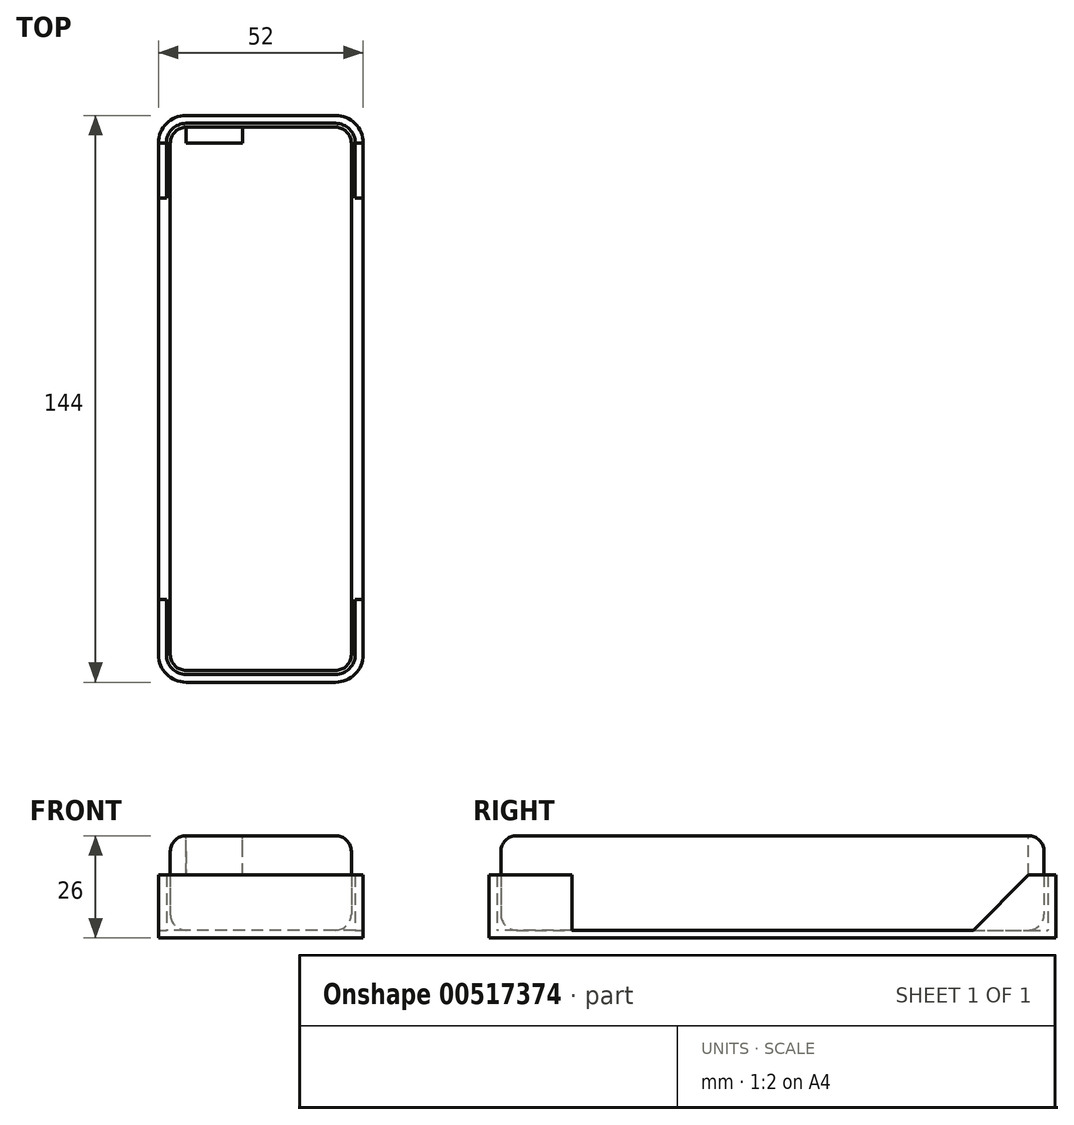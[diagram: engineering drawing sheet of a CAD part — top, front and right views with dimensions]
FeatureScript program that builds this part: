
annotation { "Feature Type Name" : "Feature", "Feature Type Description" : "" }
export const myFeature = defineFeature(function(context is Context, id is Id, definition is map)
    precondition{}
    {
        {
            var Q0;
            Q0=qCreatedBy(makeId("Top.planeOp"),FACE);
            var sketch = newSketch(context, id + "F0", { "sketchPlane" : qUnion([Q0])});
            skLineSegment(sketch, "E0.bottom", {"start": v(-4, 0) * mm, "end": v(-42, 0) * mm});
            skLineSegment(sketch, "E0.top", {"start": v(-4, 138) * mm, "end": v(-42, 138) * mm});
            skLineSegment(sketch, "E0.left", {"start": v(0, 4) * mm, "end": v(0, 134) * mm});
            skLineSegment(sketch, "E0.right", {"start": v(-46, 4) * mm, "end": v(-46, 134) * mm});
            skPoint(sketch, "E1.visualSharp", {"position": v(-46, 0) * mm});
            skArc(sketch, "E1.filletArc", {"start": v(-46, 4) * mm, "mid": v(-44.83, 1.17) * mm, "end": v(-42, 0) * mm});
            skPoint(sketch, "E2.visualSharp", {"position": v(0, 0) * mm});
            skArc(sketch, "E2.filletArc", {"start": v(-4, 0) * mm, "mid": v(-1.17, 1.17) * mm, "end": v(0, 4) * mm});
            skPoint(sketch, "E3.visualSharp", {"position": v(-46, 138) * mm});
            skArc(sketch, "E3.filletArc", {"start": v(-42, 138) * mm, "mid": v(-44.83, 136.83) * mm, "end": v(-46, 134) * mm});
            skPoint(sketch, "E4.visualSharp", {"position": v(0, 138) * mm});
            skArc(sketch, "E4.filletArc", {"start": v(0, 134) * mm, "mid": v(-1.17, 136.83) * mm, "end": v(-4, 138) * mm});
            skArc(sketch, "E5.0", {"start": v(-4, -3) * mm, "mid": v(0.95, -0.95) * mm, "end": v(3, 4) * mm});
            skLineSegment(sketch, "E5.1", {"start": v(-4, -3) * mm, "end": v(-42, -3) * mm});
            skLineSegment(sketch, "E5.2", {"start": v(3, 4) * mm, "end": v(3, 134) * mm});
            skArc(sketch, "E5.3", {"start": v(-49, 4) * mm, "mid": v(-46.95, -0.95) * mm, "end": v(-42, -3) * mm});
            skArc(sketch, "E5.4", {"start": v(3, 134) * mm, "mid": v(0.95, 138.95) * mm, "end": v(-4, 141) * mm});
            skLineSegment(sketch, "E5.5", {"start": v(-4, 141) * mm, "end": v(-42, 141) * mm});
            skArc(sketch, "E5.6", {"start": v(-42, 141) * mm, "mid": v(-46.95, 138.95) * mm, "end": v(-49, 134) * mm});
            skLineSegment(sketch, "E5.7", {"start": v(-49, 4) * mm, "end": v(-49, 134) * mm});
            skArc(sketch, "E6.0", {"start": v(-47, 4) * mm, "mid": v(-45.54, 0.46) * mm, "end": v(-42, -1) * mm});
            skLineSegment(sketch, "E6.1", {"start": v(-4, -1) * mm, "end": v(-42, -1) * mm});
            skLineSegment(sketch, "E6.2", {"start": v(-47, 4) * mm, "end": v(-47, 134) * mm});
            skArc(sketch, "E6.3", {"start": v(-4, -1) * mm, "mid": v(-0.46, 0.46) * mm, "end": v(1, 4) * mm});
            skArc(sketch, "E6.4", {"start": v(-42, 139) * mm, "mid": v(-45.54, 137.54) * mm, "end": v(-47, 134) * mm});
            skLineSegment(sketch, "E6.5", {"start": v(-4, 139) * mm, "end": v(-42, 139) * mm});
            skArc(sketch, "E6.6", {"start": v(1, 134) * mm, "mid": v(-0.46, 137.54) * mm, "end": v(-4, 139) * mm});
            skLineSegment(sketch, "E6.7", {"start": v(1, 4) * mm, "end": v(1, 134) * mm});
            skSolve(sketch);
        }
        {
            var Q0;
            Q0=makeQuery(id+"F0.imprint","IMPRINT",FACE,{"disambiguationData":[TD([[makeQuery(id+"F0.imprint","IMPRINT",EDGE,{"derivedFrom":sQuery(id+"F0.wireOp",EDGE,"E0.bottom")}),-1.0]])]});
            extrude(context, id + "F1", {"entities" : qUnion([Q0]), "depth" : 24 * mm, "offsetDistance" : 25 * mm});
        }
        {
            var Q0;
            Q0=makeQuery(id+"F1.opExtrude","CAP_FACE",FACE,{"disambiguationData":[OSD([sQuery(id+"F0.wireOp",EDGE,"E0.bottom"),sQuery(id+"F0.wireOp",EDGE,"E0.top"),sQuery(id+"F0.wireOp",EDGE,"E0.left"),sQuery(id+"F0.wireOp",EDGE,"E0.right"),sQuery(id+"F0.wireOp",EDGE,"E1.filletArc"),sQuery(id+"F0.wireOp",EDGE,"E2.filletArc"),sQuery(id+"F0.wireOp",EDGE,"E3.filletArc"),sQuery(id+"F0.wireOp",EDGE,"E4.filletArc")])],"isStart":false});
            var Q1;
            Q1=makeQuery(id+"F1.opExtrude","CAP_FACE",FACE,{"disambiguationData":[OSD([sQuery(id+"F0.wireOp",EDGE,"E0.bottom"),sQuery(id+"F0.wireOp",EDGE,"E0.top"),sQuery(id+"F0.wireOp",EDGE,"E0.left"),sQuery(id+"F0.wireOp",EDGE,"E0.right"),sQuery(id+"F0.wireOp",EDGE,"E1.filletArc"),sQuery(id+"F0.wireOp",EDGE,"E2.filletArc"),sQuery(id+"F0.wireOp",EDGE,"E3.filletArc"),sQuery(id+"F0.wireOp",EDGE,"E4.filletArc")])],"isStart":true});
            fillet(context, id + "F2", {"entities" : qUnion([Q0, Q1]), "radius" : 4 * mm, "tangentPropagation" : true, "allowEdgeOverflow" : false});
        }
        {
            var Q0;
            Q0=makeQuery(id+"F1.opExtrude","CAP_FACE",FACE,{"disambiguationData":[OSD([sQuery(id+"F0.wireOp",EDGE,"E0.bottom"),sQuery(id+"F0.wireOp",EDGE,"E0.top"),sQuery(id+"F0.wireOp",EDGE,"E0.left"),sQuery(id+"F0.wireOp",EDGE,"E0.right"),sQuery(id+"F0.wireOp",EDGE,"E1.filletArc"),sQuery(id+"F0.wireOp",EDGE,"E2.filletArc"),sQuery(id+"F0.wireOp",EDGE,"E3.filletArc"),sQuery(id+"F0.wireOp",EDGE,"E4.filletArc")])],"isStart":false});
            var sketch = newSketch(context, id + "F3", { "sketchPlane" : qUnion([Q0])});
            skLineSegment(sketch, "E7.bottom", {"start": v(-42, 134) * mm, "end": v(-27.63, 134) * mm});
            skLineSegment(sketch, "E7.top", {"start": v(-42, 138.18) * mm, "end": v(-27.63, 138.18) * mm});
            skLineSegment(sketch, "E7.left", {"start": v(-42, 134) * mm, "end": v(-42, 138.18) * mm});
            skLineSegment(sketch, "E7.right", {"start": v(-27.63, 134) * mm, "end": v(-27.63, 138.18) * mm});
            skSolve(sketch);
        }
        {
            var Q0;
            Q0=makeQuery(id+"F3.imprint","IMPRINT",FACE,{"disambiguationData":[TD([[makeQuery(id+"F3.imprint","IMPRINT",EDGE,{"derivedFrom":sQuery(id+"F3.wireOp",EDGE,"E7.bottom")}),-1.0]])]});
            extrude(context, id + "F4", {"entities" : qUnion([Q0]), "operationType" : NewBodyOperationType.REMOVE, "oppositeDirection" : true, "depth" : 10 * mm, "offsetDistance" : 25 * mm});
        }
        {
            var Q0;
            Q0=makeQuery(id+"F0.imprint","IMPRINT",FACE,{"disambiguationData":[TD([[makeQuery(id+"F0.imprint","IMPRINT",EDGE,{"derivedFrom":sQuery(id+"F0.wireOp",EDGE,"E5.0")}),1.0]])]});
            extrude(context, id + "F5", {"entities" : qUnion([Q0]), "depth" : 14 * mm, "offsetDistance" : 25 * mm});
        }
        {
            var Q0;
            Q0=makeQuery(id+"F0.imprint","IMPRINT",FACE,{"disambiguationData":[TD([[makeQuery(id+"F0.imprint","IMPRINT",EDGE,{"derivedFrom":sQuery(id+"F0.wireOp",EDGE,"E5.0")}),1.0]])]});
            var Q1;
            Q1=makeQuery(id+"F0.imprint","IMPRINT",FACE,{"disambiguationData":[TD([[makeQuery(id+"F0.imprint","IMPRINT",EDGE,{"derivedFrom":sQuery(id+"F0.wireOp",EDGE,"E0.bottom")}),-1.0]])]});
            extrude(context, id + "F6", {"entities" : qUnion([Q0, Q1]), "oppositeDirection" : true, "depth" : 2 * mm, "offsetDistance" : 25 * mm});
        }
        {
            var Q0;
            Q0=makeQuery(id+"F0.imprint","IMPRINT",FACE,{"disambiguationData":[TD([[makeQuery(id+"F0.imprint","IMPRINT",EDGE,{"derivedFrom":sQuery(id+"F0.wireOp",EDGE,"E0.bottom")}),1.0]])]});
            extrude(context, id + "F7", {"entities" : qUnion([Q0]), "operationType" : NewBodyOperationType.ADD, "oppositeDirection" : true, "depth" : 2 * mm, "offsetDistance" : 25 * mm});
        }
        {
            var Q0;
            Q0=makeQuery(id+"F5.opExtrude","CAP_FACE",FACE,{"disambiguationData":[OSD([sQuery(id+"F0.wireOp",EDGE,"E5.0"),sQuery(id+"F0.wireOp",EDGE,"E5.1"),sQuery(id+"F0.wireOp",EDGE,"E5.2"),sQuery(id+"F0.wireOp",EDGE,"E5.3"),sQuery(id+"F0.wireOp",EDGE,"E5.4"),sQuery(id+"F0.wireOp",EDGE,"E5.5"),sQuery(id+"F0.wireOp",EDGE,"E5.6"),sQuery(id+"F0.wireOp",EDGE,"E5.7"),sQuery(id+"F0.wireOp",EDGE,"E6.0"),sQuery(id+"F0.wireOp",EDGE,"E6.1"),sQuery(id+"F0.wireOp",EDGE,"E6.2"),sQuery(id+"F0.wireOp",EDGE,"E6.3"),sQuery(id+"F0.wireOp",EDGE,"E6.4"),sQuery(id+"F0.wireOp",EDGE,"E6.5"),sQuery(id+"F0.wireOp",EDGE,"E6.6"),sQuery(id+"F0.wireOp",EDGE,"E6.7")])],"isStart":false});
            var sketch = newSketch(context, id + "F8", { "sketchPlane" : qUnion([Q0])});
            skLineSegment(sketch, "E8.bottom", {"start": v(-49, 134) * mm, "end": v(3, 134) * mm});
            skLineSegment(sketch, "E8.top", {"start": v(-49, 4) * mm, "end": v(3, 4) * mm});
            skLineSegment(sketch, "E8.left", {"start": v(-49, 134) * mm, "end": v(-49, 4) * mm});
            skLineSegment(sketch, "E8.right", {"start": v(3, 134) * mm, "end": v(3, 4) * mm});
            skSolve(sketch);
        }
        {
            var Q0;
            {var subQ0=sQuery(id+"F8.wireOp",EDGE,"E8.left");Q0=makeQuery(id+"F8.imprint","IMPRINT",FACE,{"disambiguationData":[TD([[makeQuery(id+"F8.imprint","IMPRINT",EDGE,{"derivedFrom":subQ0}),-1.0]])]});}
            var Q1;
            {var subQ0=sQuery(id+"F8.wireOp",EDGE,"E8.right");Q1=makeQuery(id+"F8.imprint","IMPRINT",FACE,{"disambiguationData":[TD([[makeQuery(id+"F8.imprint","IMPRINT",EDGE,{"derivedFrom":subQ0}),1.0]])]});}
            extrude(context, id + "F9", {"entities" : qUnion([Q0, Q1]), "operationType" : NewBodyOperationType.REMOVE, "oppositeDirection" : true, "depth" : 14 * mm, "offsetDistance" : 25 * mm});
        }
        {
            var Q0;
            {var subQ0=sQuery(id+"F8.wireOp",EDGE,"E8.top");Q0=makeQuery(id+"F9.boolean.opBoolean","COPY",FACE,{"derivedFrom":makeQuery(id+"F9.opExtrude","SWEPT_FACE",FACE,{"disambiguationData":[OSD([subQ0]),TDD([makeQuery(id+"F8.imprint","IMPRINT",EDGE,{"disambiguationData":[TD([[makeQuery(id+"F8.imprint","INTERSECT",VERTEX,{"derivedFrom":[makeQuery(id+"F5.opExtrude","CAP_EDGE",EDGE,{"disambiguationData":[OSD([sQuery(id+"F0.wireOp",EDGE,"E5.3")])],"isStart":false}),subQ0,sQuery(id+"F8.wireOp",EDGE,"E8.left")]}),-1.0]])],"derivedFrom":subQ0})])]})});}
            var Q1;
            {var subQ0=sQuery(id+"F8.wireOp",EDGE,"E8.top");Q1=makeQuery(id+"F9.boolean.opBoolean","COPY",FACE,{"derivedFrom":makeQuery(id+"F9.opExtrude","SWEPT_FACE",FACE,{"disambiguationData":[OSD([subQ0]),TDD([makeQuery(id+"F8.imprint","IMPRINT",EDGE,{"disambiguationData":[TD([[makeQuery(id+"F8.imprint","INTERSECT",VERTEX,{"derivedFrom":[makeQuery(id+"F5.opExtrude","CAP_EDGE",EDGE,{"disambiguationData":[OSD([sQuery(id+"F0.wireOp",EDGE,"E5.0")])],"isStart":false}),subQ0,sQuery(id+"F8.wireOp",EDGE,"E8.right")]}),1.0]])],"derivedFrom":subQ0})])]})});}
            extrude(context, id + "F10", {"entities" : qUnion([Q0, Q1]), "operationType" : NewBodyOperationType.ADD, "depth" : 14 * mm, "offsetDistance" : 25 * mm});
        }
        {
            var Q0;
            {var subQ0=sQuery(id+"F8.wireOp",EDGE,"E8.bottom");Q0=makeQuery(id+"F9.boolean.opBoolean","COPY",FACE,{"derivedFrom":makeQuery(id+"F9.opExtrude","SWEPT_FACE",FACE,{"disambiguationData":[OSD([subQ0]),TDD([makeQuery(id+"F8.imprint","IMPRINT",EDGE,{"disambiguationData":[TD([[makeQuery(id+"F8.imprint","INTERSECT",VERTEX,{"derivedFrom":[makeQuery(id+"F5.opExtrude","CAP_EDGE",EDGE,{"disambiguationData":[OSD([sQuery(id+"F0.wireOp",EDGE,"E5.4")])],"isStart":false}),subQ0,sQuery(id+"F8.wireOp",EDGE,"E8.right")]}),1.0]])],"derivedFrom":subQ0})])]})});}
            var Q1;
            {var subQ0=sQuery(id+"F8.wireOp",EDGE,"E8.bottom");Q1=makeQuery(id+"F9.boolean.opBoolean","COPY",FACE,{"derivedFrom":makeQuery(id+"F9.opExtrude","SWEPT_FACE",FACE,{"disambiguationData":[OSD([subQ0]),TDD([makeQuery(id+"F8.imprint","IMPRINT",EDGE,{"disambiguationData":[TD([[makeQuery(id+"F8.imprint","INTERSECT",VERTEX,{"derivedFrom":[makeQuery(id+"F5.opExtrude","CAP_EDGE",EDGE,{"disambiguationData":[OSD([sQuery(id+"F0.wireOp",EDGE,"E5.6")])],"isStart":false}),subQ0,sQuery(id+"F8.wireOp",EDGE,"E8.left")]}),-1.0]])],"derivedFrom":subQ0})])]})});}
            extrude(context, id + "F11", {"entities" : qUnion([Q0, Q1]), "operationType" : NewBodyOperationType.ADD, "depth" : 14 * mm, "offsetDistance" : 25 * mm});
        }
        {
            var Q0;
            {var subQ0=sQuery(id+"F8.wireOp",EDGE,"E8.bottom");Q0=makeQuery(id+"F11.opExtrude","CAP_EDGE",EDGE,{"disambiguationData":[OSD([subQ0]),TDD([makeQuery(id+"F9.boolean.opBoolean","COPY",EDGE,{"derivedFrom":makeQuery(id+"F9.opExtrude","CAP_EDGE",EDGE,{"disambiguationData":[OSD([subQ0]),TDD([makeQuery(id+"F8.imprint","IMPRINT",EDGE,{"disambiguationData":[TD([[makeQuery(id+"F8.imprint","INTERSECT",VERTEX,{"derivedFrom":[makeQuery(id+"F5.opExtrude","CAP_EDGE",EDGE,{"disambiguationData":[OSD([sQuery(id+"F0.wireOp",EDGE,"E5.6")])],"isStart":false}),subQ0,sQuery(id+"F8.wireOp",EDGE,"E8.left")]}),-1.0]])],"derivedFrom":subQ0})])],"isStart":true})})])],"isStart":false});}
            var Q1;
            {var subQ0=sQuery(id+"F8.wireOp",EDGE,"E8.bottom");Q1=makeQuery(id+"F11.opExtrude","CAP_EDGE",EDGE,{"disambiguationData":[OSD([subQ0]),TDD([makeQuery(id+"F9.boolean.opBoolean","COPY",EDGE,{"derivedFrom":makeQuery(id+"F9.opExtrude","CAP_EDGE",EDGE,{"disambiguationData":[OSD([subQ0]),TDD([makeQuery(id+"F8.imprint","IMPRINT",EDGE,{"disambiguationData":[TD([[makeQuery(id+"F8.imprint","INTERSECT",VERTEX,{"derivedFrom":[makeQuery(id+"F5.opExtrude","CAP_EDGE",EDGE,{"disambiguationData":[OSD([sQuery(id+"F0.wireOp",EDGE,"E5.4")])],"isStart":false}),subQ0,sQuery(id+"F8.wireOp",EDGE,"E8.right")]}),1.0]])],"derivedFrom":subQ0})])],"isStart":true})})])],"isStart":false});}
            var Q2;
            {var subQ0=sQuery(id+"F8.wireOp",EDGE,"E8.top");Q2=makeQuery(id+"F10.opExtrude","CAP_EDGE",EDGE,{"disambiguationData":[OSD([subQ0]),TDD([makeQuery(id+"F9.boolean.opBoolean","COPY",EDGE,{"derivedFrom":makeQuery(id+"F9.opExtrude","CAP_EDGE",EDGE,{"disambiguationData":[OSD([subQ0]),TDD([makeQuery(id+"F8.imprint","IMPRINT",EDGE,{"disambiguationData":[TD([[makeQuery(id+"F8.imprint","INTERSECT",VERTEX,{"derivedFrom":[makeQuery(id+"F5.opExtrude","CAP_EDGE",EDGE,{"disambiguationData":[OSD([sQuery(id+"F0.wireOp",EDGE,"E5.0")])],"isStart":false}),subQ0,sQuery(id+"F8.wireOp",EDGE,"E8.right")]}),1.0]])],"derivedFrom":subQ0})])],"isStart":true})})])],"isStart":false});}
            var Q3;
            {var subQ0=sQuery(id+"F8.wireOp",EDGE,"E8.top");Q3=makeQuery(id+"F10.opExtrude","CAP_EDGE",EDGE,{"disambiguationData":[OSD([subQ0]),TDD([makeQuery(id+"F9.boolean.opBoolean","COPY",EDGE,{"derivedFrom":makeQuery(id+"F9.opExtrude","CAP_EDGE",EDGE,{"disambiguationData":[OSD([subQ0]),TDD([makeQuery(id+"F8.imprint","IMPRINT",EDGE,{"disambiguationData":[TD([[makeQuery(id+"F8.imprint","INTERSECT",VERTEX,{"derivedFrom":[makeQuery(id+"F5.opExtrude","CAP_EDGE",EDGE,{"disambiguationData":[OSD([sQuery(id+"F0.wireOp",EDGE,"E5.3")])],"isStart":false}),subQ0,sQuery(id+"F8.wireOp",EDGE,"E8.left")]}),-1.0]])],"derivedFrom":subQ0})])],"isStart":true})})])],"isStart":false});}
            chamfer(context, id + "F12", {"entities" : qUnion([Q0, Q1, Q2, Q3]), "width" : 14 * mm, "tangentPropagation" : true});
        }
    });
